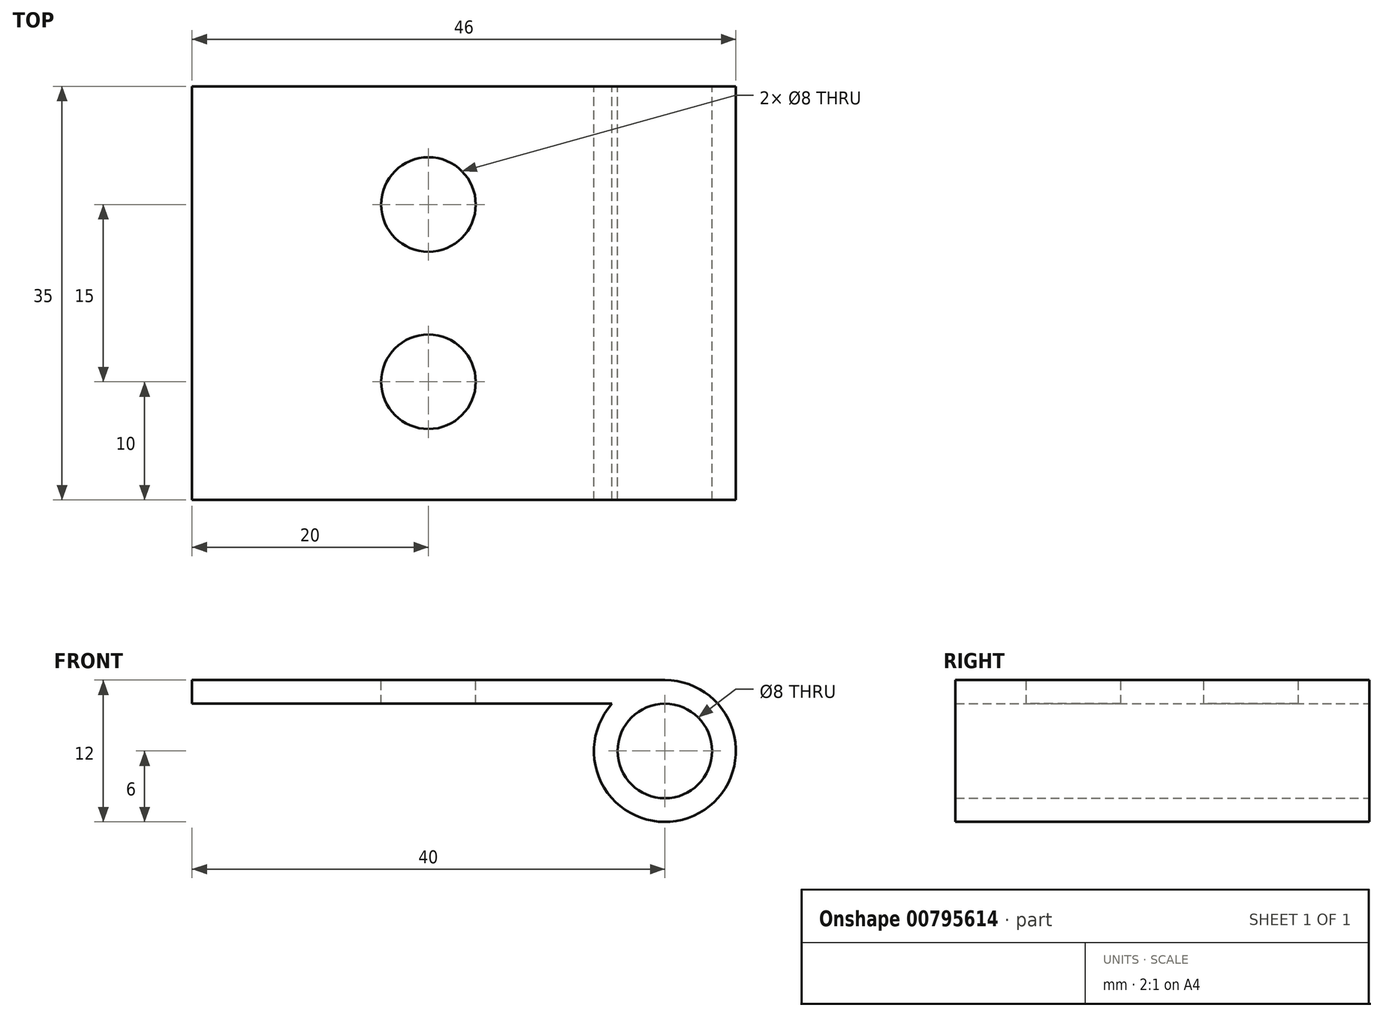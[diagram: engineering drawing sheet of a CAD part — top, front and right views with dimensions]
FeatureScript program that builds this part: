
annotation { "Feature Type Name" : "Feature", "Feature Type Description" : "" }
export const myFeature = defineFeature(function(context is Context, id is Id, definition is map)
    precondition{}
    {
        {
            var Q0;
            Q0=qCreatedBy(makeId("Front.planeOp"),FACE);
            var sketch = newSketch(context, id + "F0", { "sketchPlane" : qUnion([Q0])});
            skCircle(sketch, "E0", {"center": v(0, 0) * mm, "radius": 6 * mm});
            skLineSegment(sketch, "E1", {"start": v(0, 6) * mm, "end": v(-40, 6) * mm});
            skLineSegment(sketch, "E2", {"start": v(-40, 6) * mm, "end": v(-40, 4) * mm});
            skLineSegment(sketch, "E3", {"start": v(-40, 4) * mm, "end": v(-4.47, 4) * mm});
            skCircle(sketch, "E4", {"center": v(0, 0) * mm, "radius": 4 * mm});
            skSolve(sketch);
        }
        {
            var Q0;
            {var subQ0=sQuery(id+"F0.wireOp",EDGE,"E1");Q0=makeQuery(id+"F0.imprint","IMPRINT",FACE,{"disambiguationData":[TD([[makeQuery(id+"F0.imprint","IMPRINT",EDGE,{"derivedFrom":subQ0}),1.0]])]});}
            var Q1;
            Q1=makeQuery(id+"F0.imprint","IMPRINT",FACE,{"disambiguationData":[TD([[makeQuery(id+"F0.imprint","IMPRINT",EDGE,{"derivedFrom":sQuery(id+"F0.wireOp",EDGE,"E4")}),-1.0]])]});
            extrude(context, id + "F1", {"entities" : qUnion([Q0, Q1]), "endBound" : BoundingType.SYMMETRIC, "depth" : 35 * mm, "offsetDistance" : 25 * mm});
        }
        {
            var Q0;
            Q0=makeQuery(id+"F1.opExtrude","SWEPT_FACE",FACE,{"disambiguationData":[OSD([sQuery(id+"F0.wireOp",EDGE,"E1")])]});
            var sketch = newSketch(context, id + "F2", { "sketchPlane" : qUnion([Q0])});
            skCircle(sketch, "E5", {"center": v(-20, 7.5) * mm, "radius": 4 * mm});
            skCircle(sketch, "E6", {"center": v(-20, -7.5) * mm, "radius": 4 * mm});
            skLineSegment(sketch, "E7", {"start": v(-20, 7.5) * mm, "end": v(-20, -7.5) * mm, "construction": true});
            skSolve(sketch);
        }
        {
            var Q0;
            Q0=sQuery(id+"F2.wireOp",VERTEX,"E7.start");
            var Q1;
            Q1=sQuery(id+"F2.wireOp",VERTEX,"E7.end");
            var Q2;
            Q2=makeQuery(id+"F1.opExtrude","SWEPT_BODY",BODY,{"disambiguationData":[OSD([sQuery(id+"F0.wireOp",EDGE,"E0"),sQuery(id+"F0.wireOp",EDGE,"E1"),sQuery(id+"F0.wireOp",EDGE,"E2"),sQuery(id+"F0.wireOp",EDGE,"E3"),sQuery(id+"F0.wireOp",EDGE,"E4")])]});
            hole(context, id + "F3", {"style" : HoleStyle.SIMPLE, "endStyle" : HoleEndStyle.THROUGH, "standardTappedOrClearance" : lookupTablePath({ "standard" : "ISO", "size" : "8", "type" : "Drilled" }), "standardBlindInLast" : lookupTablePath({ "standard" : "ISO", "size" : "8", "type" : "Drilled" }), "holeDiameter" : 8 * mm, "majorDiameter" : 5 * mm, "isTappedThrough" : true, "tappedDepth" : 12.7 * mm, "tapClearance" : 3, "locations" : qUnion([Q0, Q1]), "scope" : qUnion([Q2])});
        }
    });
